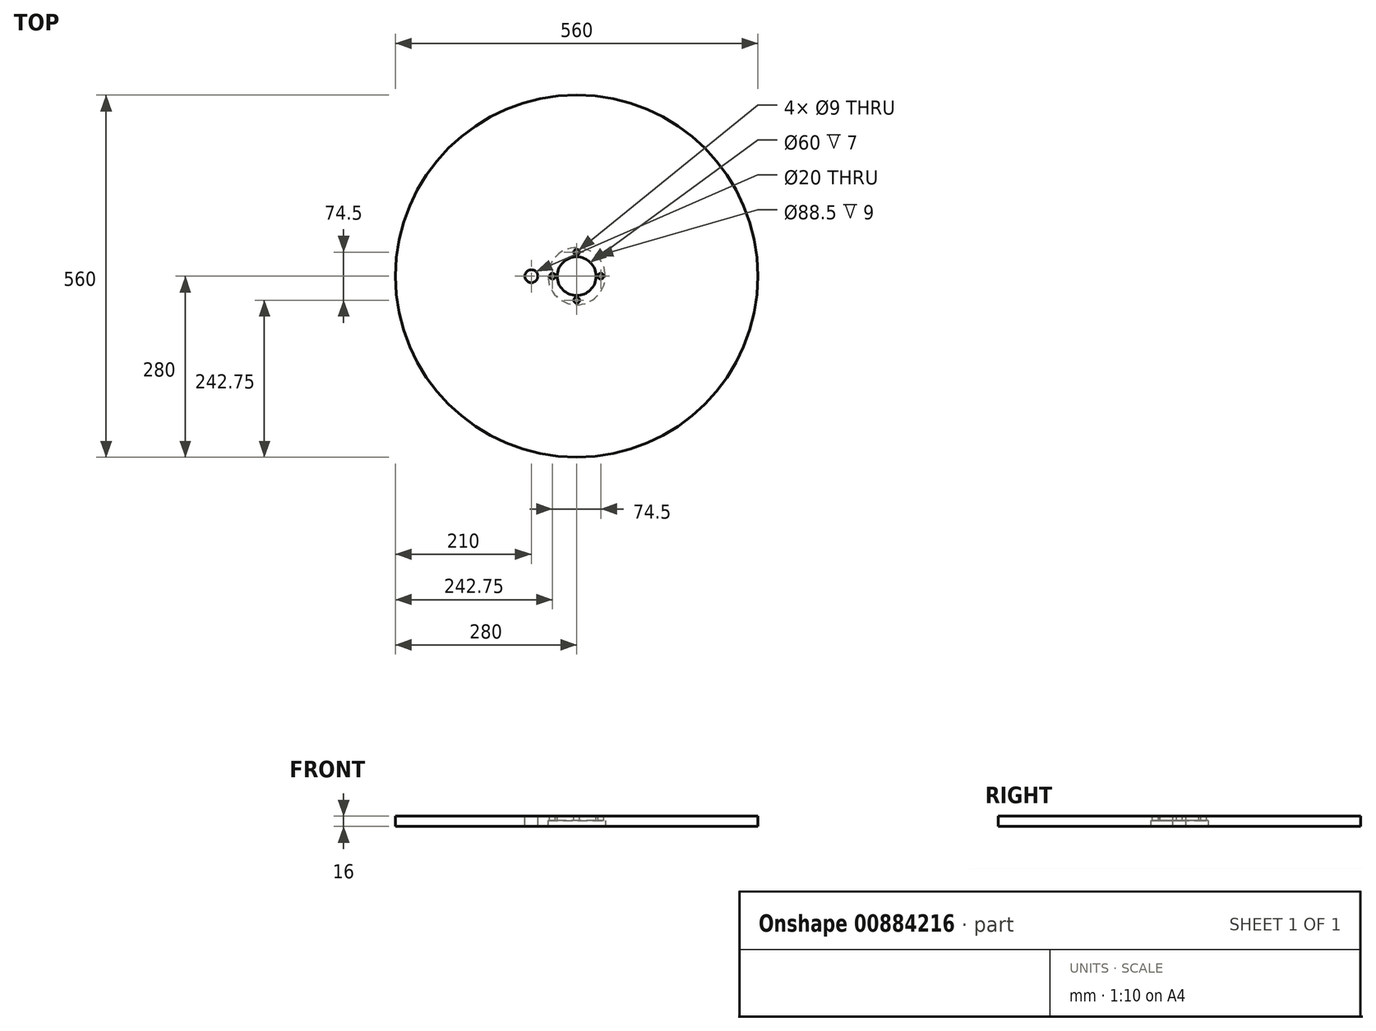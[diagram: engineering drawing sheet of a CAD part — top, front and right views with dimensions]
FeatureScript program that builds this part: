
annotation { "Feature Type Name" : "Feature", "Feature Type Description" : "" }
export const myFeature = defineFeature(function(context is Context, id is Id, definition is map)
    precondition{}
    {
        {
            var Q0;
            Q0=qCreatedBy(makeId("Top.planeOp"),FACE);
            var sketch = newSketch(context, id + "F0", { "sketchPlane" : qUnion([Q0])});
            skCircle(sketch, "E0", {"center": v(0, 0) * mm, "radius": 280 * mm});
            skSolve(sketch);
        }
        {
            var Q0;
            Q0=makeQuery(id+"F0.imprint","IMPRINT",FACE,{"disambiguationData":[TD([[makeQuery(id+"F0.imprint","IMPRINT",EDGE,{"derivedFrom":sQuery(id+"F0.wireOp",EDGE,"E0")}),1.0]])]});
            extrude(context, id + "F1", {"entities" : qUnion([Q0]), "depth" : 16 * mm, "offsetDistance" : 25 * mm});
        }
        {
            var Q0;
            Q0=makeQuery(id+"F1.opExtrude","CAP_FACE",FACE,{"disambiguationData":[OSD([sQuery(id+"F0.wireOp",EDGE,"E0")])],"isStart":false});
            var sketch = newSketch(context, id + "F2", { "sketchPlane" : qUnion([Q0])});
            skCircle(sketch, "E1", {"center": v(0, 0) * mm, "radius": 30 * mm});
            skCircle(sketch, "E2", {"center": v(0, 0) * mm, "radius": 70 * mm, "construction": true});
            skCircle(sketch, "E3", {"center": v(-70, 0) * mm, "radius": 10 * mm});
            skCircle(sketch, "E4", {"center": v(0, 0) * mm, "radius": 37.25 * mm, "construction": true});
            skCircle(sketch, "E5", {"center": v(0, 37.25) * mm, "radius": 4.5 * mm});
            skCircle(sketch, "E6", {"center": v(-37.25, 0) * mm, "radius": 4.5 * mm});
            skCircle(sketch, "E7", {"center": v(37.25, 0) * mm, "radius": 4.5 * mm});
            skCircle(sketch, "E8", {"center": v(0, -37.25) * mm, "radius": 4.5 * mm});
            skSolve(sketch);
        }
        {
            var Q0;
            Q0=makeQuery(id+"F2.imprint","IMPRINT",FACE,{"disambiguationData":[TD([[makeQuery(id+"F2.imprint","IMPRINT",EDGE,{"derivedFrom":sQuery(id+"F2.wireOp",EDGE,"E1")}),1.0]])]});
            var Q1;
            Q1=makeQuery(id+"F2.imprint","IMPRINT",FACE,{"disambiguationData":[TD([[makeQuery(id+"F2.imprint","IMPRINT",EDGE,{"derivedFrom":sQuery(id+"F2.wireOp",EDGE,"E3")}),1.0]])]});
            var Q2;
            Q2=makeQuery(id+"F2.imprint","IMPRINT",FACE,{"disambiguationData":[TD([[makeQuery(id+"F2.imprint","IMPRINT",EDGE,{"derivedFrom":sQuery(id+"F2.wireOp",EDGE,"E6")}),1.0]])]});
            var Q3;
            Q3=makeQuery(id+"F2.imprint","IMPRINT",FACE,{"disambiguationData":[TD([[makeQuery(id+"F2.imprint","IMPRINT",EDGE,{"derivedFrom":sQuery(id+"F2.wireOp",EDGE,"E5")}),1.0]])]});
            var Q4;
            Q4=makeQuery(id+"F2.imprint","IMPRINT",FACE,{"disambiguationData":[TD([[makeQuery(id+"F2.imprint","IMPRINT",EDGE,{"derivedFrom":sQuery(id+"F2.wireOp",EDGE,"E7")}),1.0]])]});
            var Q5;
            Q5=makeQuery(id+"F2.imprint","IMPRINT",FACE,{"disambiguationData":[TD([[makeQuery(id+"F2.imprint","IMPRINT",EDGE,{"derivedFrom":sQuery(id+"F2.wireOp",EDGE,"E8")}),1.0]])]});
            extrude(context, id + "F3", {"entities" : qUnion([Q0, Q1, Q2, Q3, Q4, Q5]), "operationType" : NewBodyOperationType.REMOVE, "oppositeDirection" : true, "depth" : 25 * mm, "offsetDistance" : 25 * mm});
        }
        {
            var Q0;
            Q0=makeQuery(id+"F1.opExtrude","CAP_FACE",FACE,{"disambiguationData":[OSD([sQuery(id+"F0.wireOp",EDGE,"E0")])],"isStart":true});
            var sketch = newSketch(context, id + "F4", { "sketchPlane" : qUnion([Q0])});
            skCircle(sketch, "E9", {"center": v(0, 0) * mm, "radius": 44.25 * mm});
            skSolve(sketch);
        }
        {
            var Q0;
            Q0=makeQuery(id+"F4.imprint","IMPRINT",FACE,{"disambiguationData":[TD([[makeQuery(id+"F4.imprint","IMPRINT",EDGE,{"derivedFrom":sQuery(id+"F4.wireOp",EDGE,"E9")}),1.0]])]});
            extrude(context, id + "F5", {"entities" : qUnion([Q0]), "operationType" : NewBodyOperationType.REMOVE, "oppositeDirection" : true, "depth" : 9 * mm, "offsetDistance" : 25 * mm});
        }
    });
